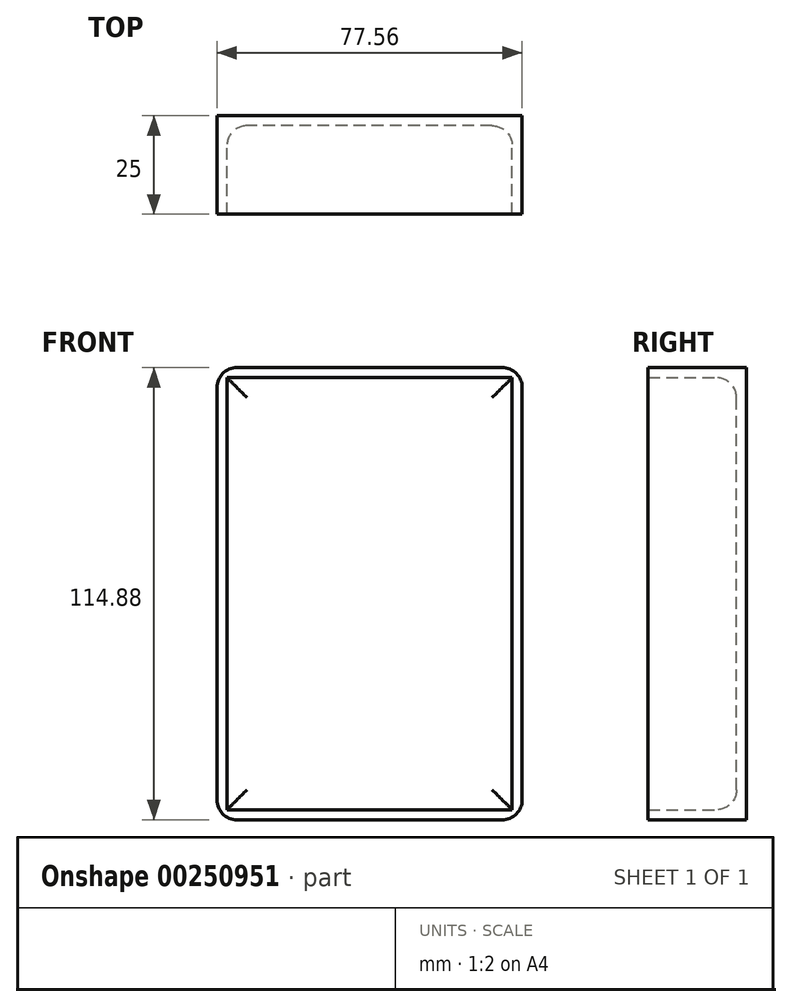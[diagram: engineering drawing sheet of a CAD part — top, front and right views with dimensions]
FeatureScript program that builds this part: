
annotation { "Feature Type Name" : "Feature", "Feature Type Description" : "" }
export const myFeature = defineFeature(function(context is Context, id is Id, definition is map)
    precondition{}
    {
        {
            var Q0;
            Q0=qCreatedBy(makeId("Front.planeOp"),FACE);
            var sketch = newSketch(context, id + "F0", { "sketchPlane" : qUnion([Q0])});
            skLineSegment(sketch, "E0.bottom", {"start": v(38.78, -57.44) * mm, "end": v(-38.78, -57.44) * mm});
            skLineSegment(sketch, "E0.top", {"start": v(38.78, 57.44) * mm, "end": v(-38.78, 57.44) * mm});
            skLineSegment(sketch, "E0.left", {"start": v(38.78, -57.44) * mm, "end": v(38.78, 57.44) * mm});
            skLineSegment(sketch, "E0.right", {"start": v(-38.78, -57.44) * mm, "end": v(-38.78, 57.44) * mm});
            skPoint(sketch, "E0.middle", {"position": v(0, 0) * mm});
            skSolve(sketch);
        }
        {
            var Q0;
            Q0=makeQuery(id+"F0.imprint","IMPRINT",FACE,{"disambiguationData":[TD([[makeQuery(id+"F0.imprint","IMPRINT",EDGE,{"derivedFrom":sQuery(id+"F0.wireOp",EDGE,"E0.bottom")}),-1.0]])]});
            extrude(context, id + "F1", {"entities" : qUnion([Q0]), "endBound" : BoundingType.SYMMETRIC, "depth" : 25 * mm});
        }
        {
            var Q0;
            Q0=makeQuery(id+"F1.opExtrude","CAP_FACE",FACE,{"disambiguationData":[OSD([sQuery(id+"F0.wireOp",EDGE,"E0.bottom"),sQuery(id+"F0.wireOp",EDGE,"E0.top"),sQuery(id+"F0.wireOp",EDGE,"E0.left"),sQuery(id+"F0.wireOp",EDGE,"E0.right")])],"isStart":false});
            shell(context, id + "F2", {"entities" : qUnion([Q0]), "thickness" : 2.54 * mm});
        }
        {
            var Q0;
            Q0=makeQuery(id+"F2.opShell","OFFSET_FACE",FACE,{"disambiguationData":[OSD([sQuery(id+"F0.wireOp",EDGE,"E0.bottom"),sQuery(id+"F0.wireOp",EDGE,"E0.top"),sQuery(id+"F0.wireOp",EDGE,"E0.left"),sQuery(id+"F0.wireOp",EDGE,"E0.right")])]});
            fillet(context, id + "F3", {"entities" : qUnion([Q0]), "radius" : 5.08 * mm, "tangentPropagation" : true, "allowEdgeOverflow" : false});
        }
        {
            var Q0;
            Q0=makeQuery(id+"F1.opExtrude","SWEPT_EDGE",EDGE,{"disambiguationData":[OSD([sQuery(id+"F0.wireOp",EDGE,"E0.top"),sQuery(id+"F0.wireOp",EDGE,"E0.right")])]});
            var Q1;
            Q1=makeQuery(id+"F1.opExtrude","SWEPT_EDGE",EDGE,{"disambiguationData":[OSD([sQuery(id+"F0.wireOp",EDGE,"E0.top"),sQuery(id+"F0.wireOp",EDGE,"E0.left")])]});
            var Q2;
            Q2=makeQuery(id+"F1.opExtrude","SWEPT_EDGE",EDGE,{"disambiguationData":[OSD([sQuery(id+"F0.wireOp",EDGE,"E0.bottom"),sQuery(id+"F0.wireOp",EDGE,"E0.left")])]});
            var Q3;
            Q3=makeQuery(id+"F1.opExtrude","SWEPT_EDGE",EDGE,{"disambiguationData":[OSD([sQuery(id+"F0.wireOp",EDGE,"E0.bottom"),sQuery(id+"F0.wireOp",EDGE,"E0.right")])]});
            fillet(context, id + "F4", {"entities" : qUnion([Q0, Q1, Q2, Q3]), "radius" : 5.08 * mm, "tangentPropagation" : true, "allowEdgeOverflow" : false});
        }
    });
